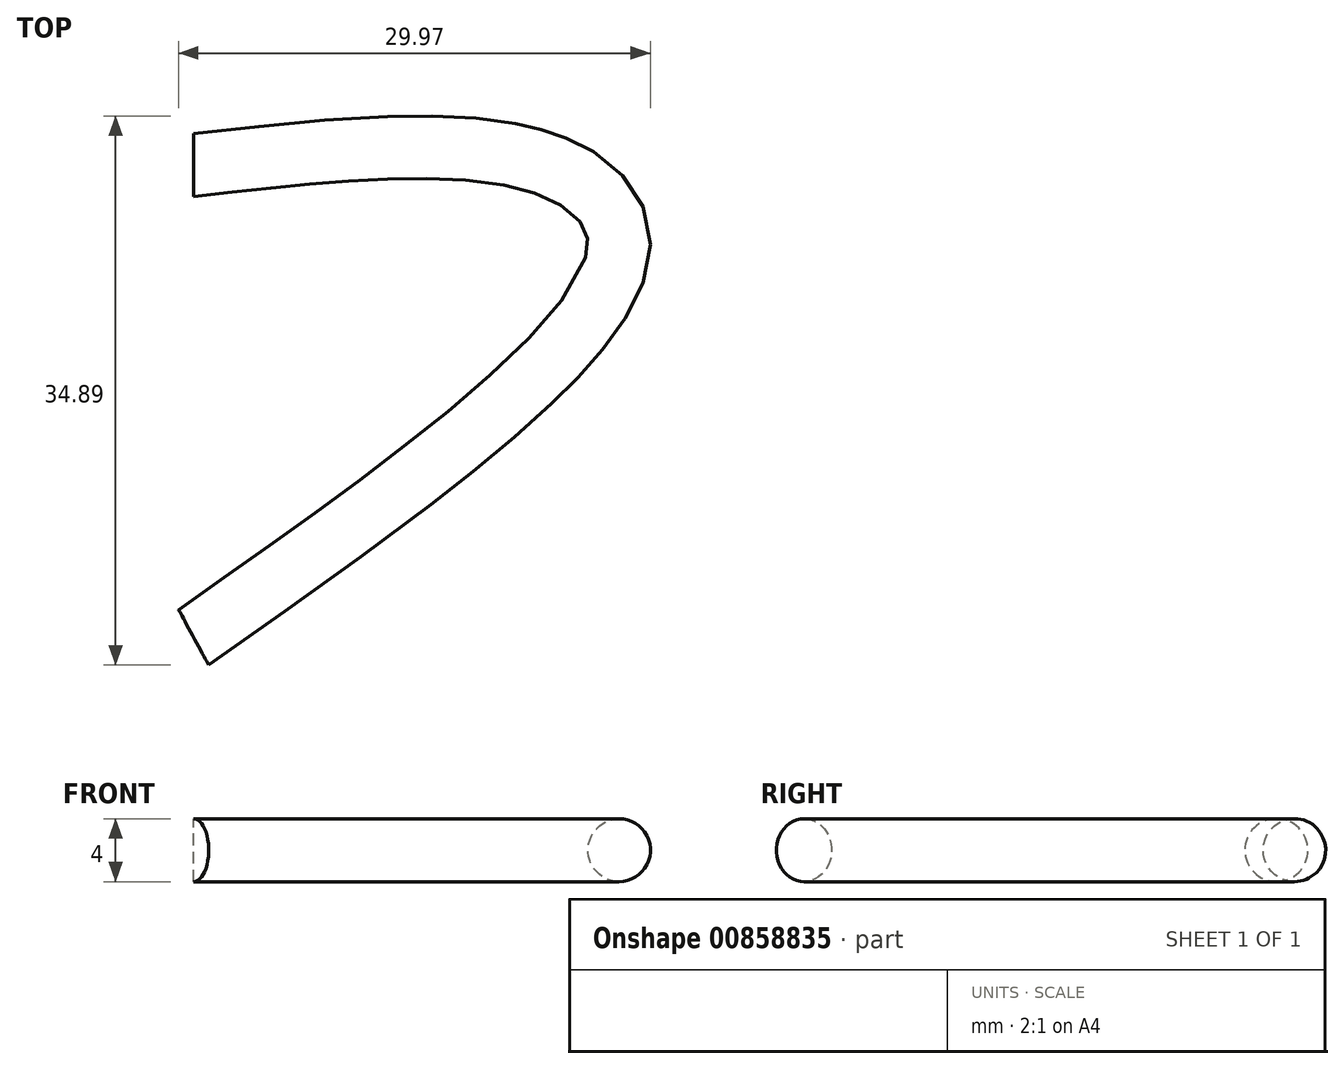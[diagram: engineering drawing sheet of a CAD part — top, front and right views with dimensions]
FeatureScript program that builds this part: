
annotation { "Feature Type Name" : "Feature", "Feature Type Description" : "" }
export const myFeature = defineFeature(function(context is Context, id is Id, definition is map)
    precondition{}
    {
        {
            var Q0;
            Q0=qCreatedBy(makeId("Top.planeOp"),FACE);
            var sketch = newSketch(context, id + "F0", { "sketchPlane" : qUnion([Q0])});
            skFitSpline(sketch, "E0", {"points": [v(0, 0) * mm, v(22.6, 0) * mm, v(26.94, -5.86) * mm, v(0, -30) * mm], "startDerivative": vector(73.77, 8.5) * mm, "endDerivative": vector(-86.7, -60.98) * mm});
            skSolve(sketch);
        }
        {
            var Q0;
            Q0=qCreatedBy(makeId("Right.planeOp"),FACE);
            var sketch = newSketch(context, id + "F1", { "sketchPlane" : qUnion([Q0])});
            skCircle(sketch, "E1", {"center": v(0, 0) * mm, "radius": 2 * mm});
            skSolve(sketch);
        }
        {
            var Q0;
            Q0=makeQuery(id+"F1.imprint","IMPRINT",FACE,{"disambiguationData":[TD([[makeQuery(id+"F1.imprint","IMPRINT",EDGE,{"derivedFrom":sQuery(id+"F1.wireOp",EDGE,"E1")}),1.0]])]});
            var Q1;
            Q1=sQuery(id+"F0.wireOp",EDGE,"E0");
            sweep(context, id + "F2", {"profiles" : qUnion([Q0]), "path" : qUnion([Q1])});
        }
    });
